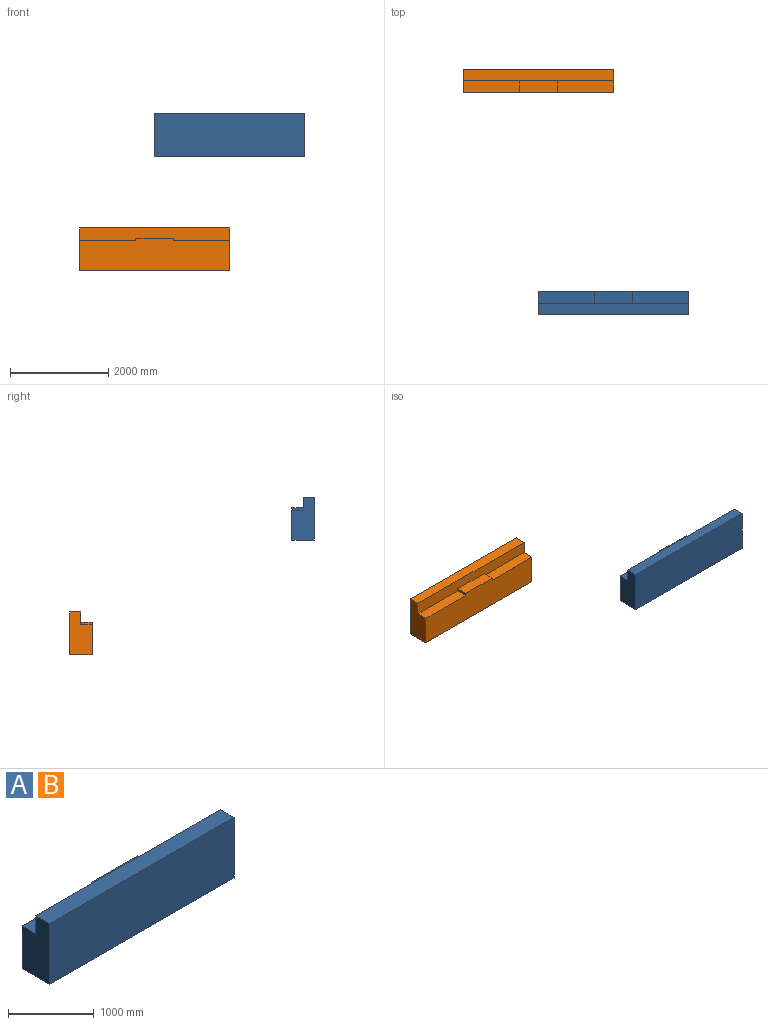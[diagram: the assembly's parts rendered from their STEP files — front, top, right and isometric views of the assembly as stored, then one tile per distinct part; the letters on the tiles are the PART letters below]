
ASSEMBLY  parts=2 mates=3
PART A: 12 faces, bbox 3048x457.2x866.1 mm
  f0: plane 1143x228.6mm, normal (0,0,1), area 261289.8mm2, adj f1,f4,f8,f9
  f1: plane 3048x256.54mm, normal (0,1,0), area 743224.3mm2, adj f0,f5,f6,f7,f8,f9,f10,f11
  f2: plane 3048x866.14mm, normal (0,-1,0), area 2639994.7mm2, adj f3,f6,f7,f8
  f3: plane 3048x457.2mm, normal (0,0,-1), area 1393545.6mm2, adj f2,f4,f7,f8
  f4: plane 3048x660.4mm, normal (0,1,0), area 1896770.4mm2, adj f0,f3,f5,f7,f8,f9,f10,f11
  f5: plane 1143x228.6mm, normal (0,0,1), area 261289.8mm2, adj f1,f4,f7,f10
  f6: plane 3048x228.6mm, normal (0,0,1), area 696772.8mm2, adj f1,f2,f7,f8
  f7: plane 866.14x457.2mm, normal (-1,0,0), area 337354.2mm2, adj f1,f2,f3,f4,f5,f6
  f8: plane 866.14x457.2mm, normal (1,0,0), area 337354.2mm2, adj f0,f1,f2,f3,f4,f6
  f9: plane 228.6x50.8mm, normal (1,0,0), area 11612.9mm2, adj f0,f1,f4,f11
  f10: plane 228.6x50.8mm, normal (-1,0,0), area 11612.9mm2, adj f1,f4,f5,f11
  f11: plane 762x228.6mm, normal (0,0,1), area 174193.2mm2, adj f1,f4,f9,f10
PART B: same geometry as A
PLACE A t=(1754.21,-4897.99,966.77)mm
PLACE B rot(axis=(0,0,1),180deg) t=(-2810.74,76.07,-1361.71)mm
MATE parallel A.f3 <-> B.f3  axis (0,0,-1) through (230.21,-4669.39,966.77)mm
MATE parallel B.f7 <-> A.f8  axis (1,0,0) through (237.26,-132.66,-981.63)mm
MATE parallel A.f4 <-> B.f4  axis (0,1,0) through (230.21,-4440.79,1278.31)mm
